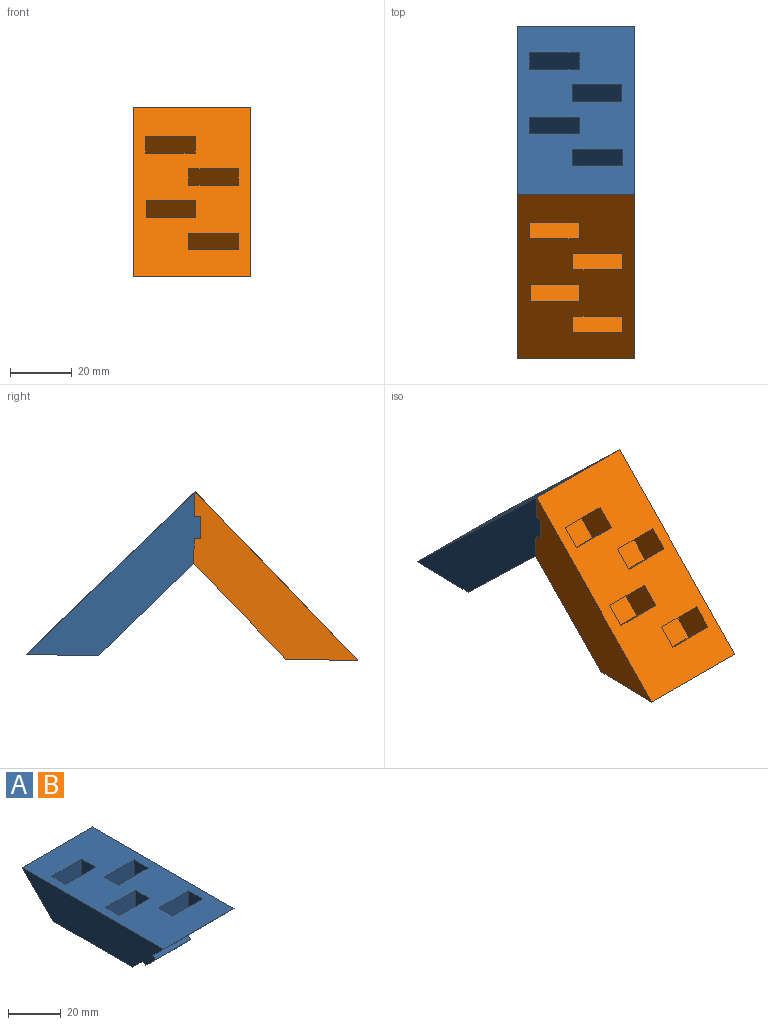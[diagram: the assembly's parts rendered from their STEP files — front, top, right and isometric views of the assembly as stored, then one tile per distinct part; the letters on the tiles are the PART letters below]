
ASSEMBLY  parts=2 mates=1
PART A: 34 faces, bbox 38x76x16.5 mm
  f0: plane 16x7.5mm, normal (0,0,1), area 120mm2, adj f4,f5,f6,f7
  f1: plane 16x7.5mm, normal (0,0,1), area 120mm2, adj f8,f9,f10,f11
  f2: plane 16x7.5mm, normal (0,0,1), area 120mm2, adj f12,f13,f14,f15
  f3: plane 16x7.5mm, normal (0,0,1), area 120mm2, adj f16,f17,f18,f19
  f4: plane 12x7.5mm, normal (1,0,0), area 90mm2, adj f0,f5,f7,f24
  f5: plane 16x12mm, normal (0,-1,0), area 192mm2, adj f0,f4,f6,f24
  f6: plane 12x7.5mm, normal (-1,0,0), area 90mm2, adj f0,f5,f7,f24
  f7: plane 16x12mm, normal (0,1,0), area 192mm2, adj f0,f4,f6,f24
  f8: plane 16x12mm, normal (0,1,0), area 192mm2, adj f1,f9,f11,f24
  f9: plane 12x7.5mm, normal (1,0,0), area 90mm2, adj f1,f8,f10,f24
  f10: plane 16x12mm, normal (0,-1,0), area 192mm2, adj f1,f9,f11,f24
  f11: plane 12x7.5mm, normal (-1,0,0), area 90mm2, adj f1,f8,f10,f24
  f12: plane 12x7.5mm, normal (1,0,0), area 90mm2, adj f2,f13,f15,f24
  f13: plane 16x12mm, normal (0,-1,0), area 192mm2, adj f2,f12,f14,f24
  f14: plane 12x7.5mm, normal (-1,0,0), area 90mm2, adj f2,f13,f15,f24
  f15: plane 16x12mm, normal (0,1,0), area 192mm2, adj f2,f12,f14,f24
  f16: plane 12x7.5mm, normal (1,0,0), area 90mm2, adj f3,f17,f19,f24
  f17: plane 16x12mm, normal (0,-1,0), area 192mm2, adj f3,f16,f18,f24
  f18: plane 12x7.5mm, normal (-1,0,0), area 90mm2, adj f3,f17,f19,f24
  f19: plane 16x12mm, normal (0,1,0), area 192mm2, adj f3,f16,f18,f24
  f20: plane 19x1.41mm, normal (0,-0.71,0.71), area 38mm2, adj f21,f25,f27,f29
  f21: plane 19x5.19mm, normal (0,-0.71,-0.71), area 139.4mm2, adj f20,f26,f27,f29
  f22: plane 19x1.41mm, normal (0,0.71,-0.71), area 38mm2, adj f25,f29,f30,f31
  f23: plane 38x16.5mm, normal (0,0.71,-0.71), area 886.7mm2, adj f24,f27,f28,f31
  f24: plane 76x38mm, normal (0,0,1), area 2408mm2, adj f4,f5,f6,f7,f8,f9,f10,f11
  f25: plane 38x5.66mm, normal (0,-0.71,-0.71), area 304mm2, adj f20,f22,f24,f27,f31
  f26: plane 19x1.41mm, normal (0,0.71,-0.71), area 38mm2, adj f21,f27,f29,f32
  f27: plane 76x16.5mm, normal (-1,0,0), area 996.4mm2, adj f20,f21,f23,f24,f25,f26,f28,f32
  f28: plane 43x38mm, normal (0,0,-1), area 1634mm2, adj f23,f27,f31,f32
  f29: plane 8.01x8.01mm, normal (1,0,0), area 29.3mm2, adj f20,f21,f22,f26,f30,f33
  f30: plane 19x5.19mm, normal (0,-0.71,-0.71), area 139.4mm2, adj f22,f29,f31,f33
  f31: plane 76x16.5mm, normal (1,0,0), area 967.1mm2, adj f22,f23,f24,f25,f28,f30,f32,f33
  f32: plane 38x5.66mm, normal (0,-0.71,-0.71), area 304mm2, adj f26,f27,f28,f31,f33
  f33: plane 19x1.41mm, normal (0,-0.71,0.71), area 38mm2, adj f29,f30,f31,f32
PART B: same geometry as A
PLACE A rot(axis=(-1,0,0),43.9deg) t=(0.62,0.57,0.31)mm
PLACE B rot(axis=(0,-0.39,0.92),180deg) t=(38.62,0.57,0.31)mm
MATE fastened A.f30 <-> B.f21  axis (0,-1,-0.02) through (29.12,2.78,-11.32)mm
